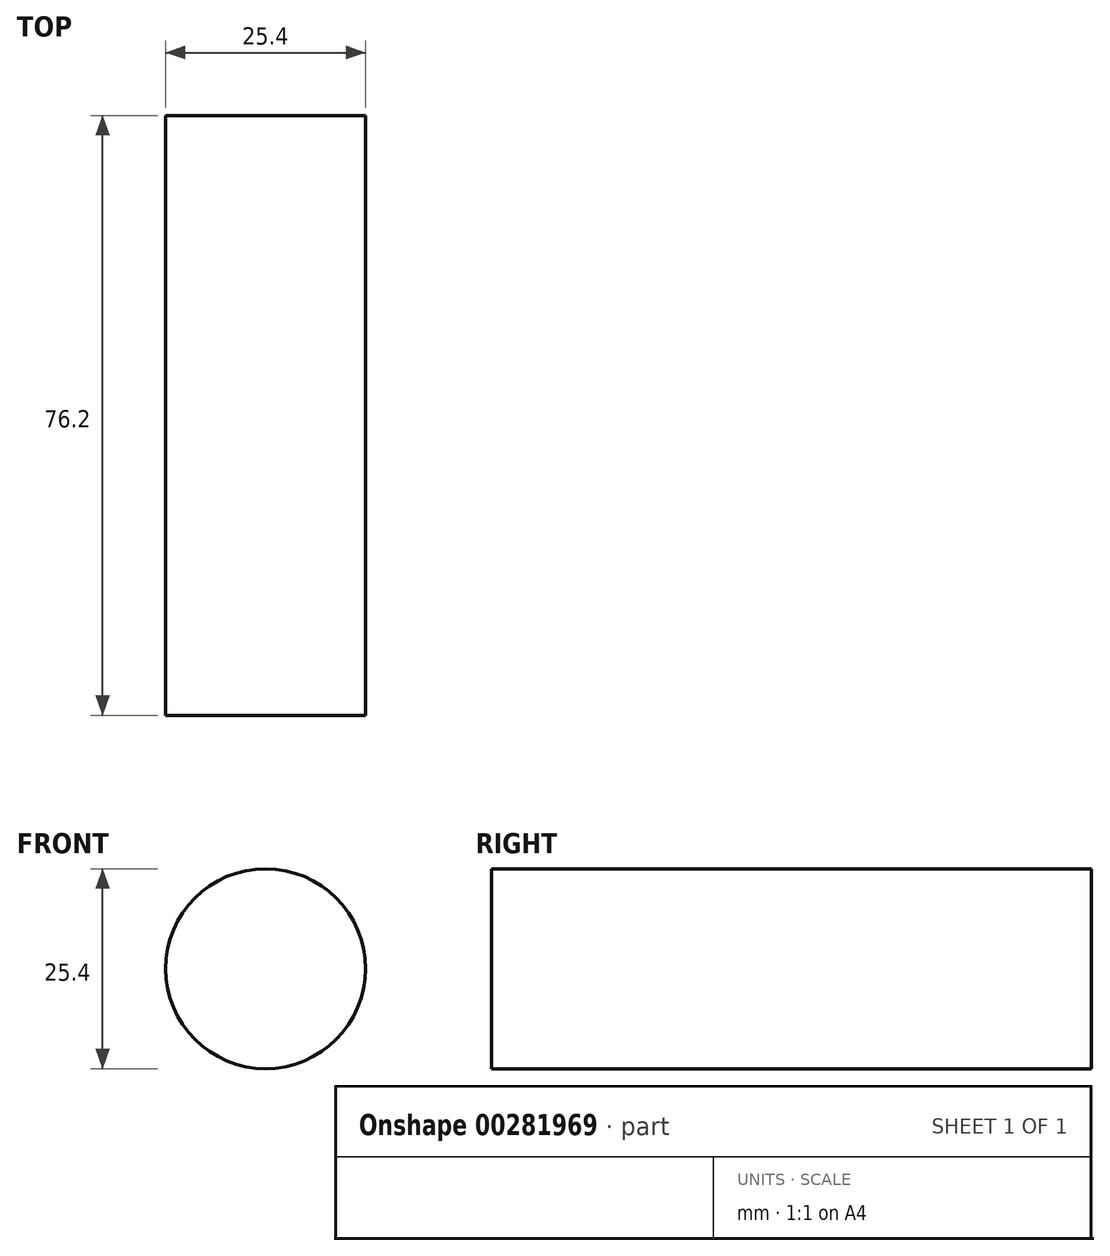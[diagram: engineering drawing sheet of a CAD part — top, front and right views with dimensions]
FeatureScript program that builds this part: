
annotation { "Feature Type Name" : "Feature", "Feature Type Description" : "" }
export const myFeature = defineFeature(function(context is Context, id is Id, definition is map)
    precondition{}
    {
        {
            var Q0;
            Q0=qCreatedBy(makeId("Front.planeOp"),FACE);
            var sketch = newSketch(context, id + "F0", { "sketchPlane" : qUnion([Q0])});
            skCircle(sketch, "E0", {"center": v(-38.64, 28.02) * mm, "radius": 12.7 * mm});
            skSolve(sketch);
        }
        {
            var Q0;
            Q0 = qSketchRegion(id + "F0", true);
            extrude(context, id + "F1", {"entities" : qUnion([Q0]), "depth" : 76.2 * mm});
        }
    });
